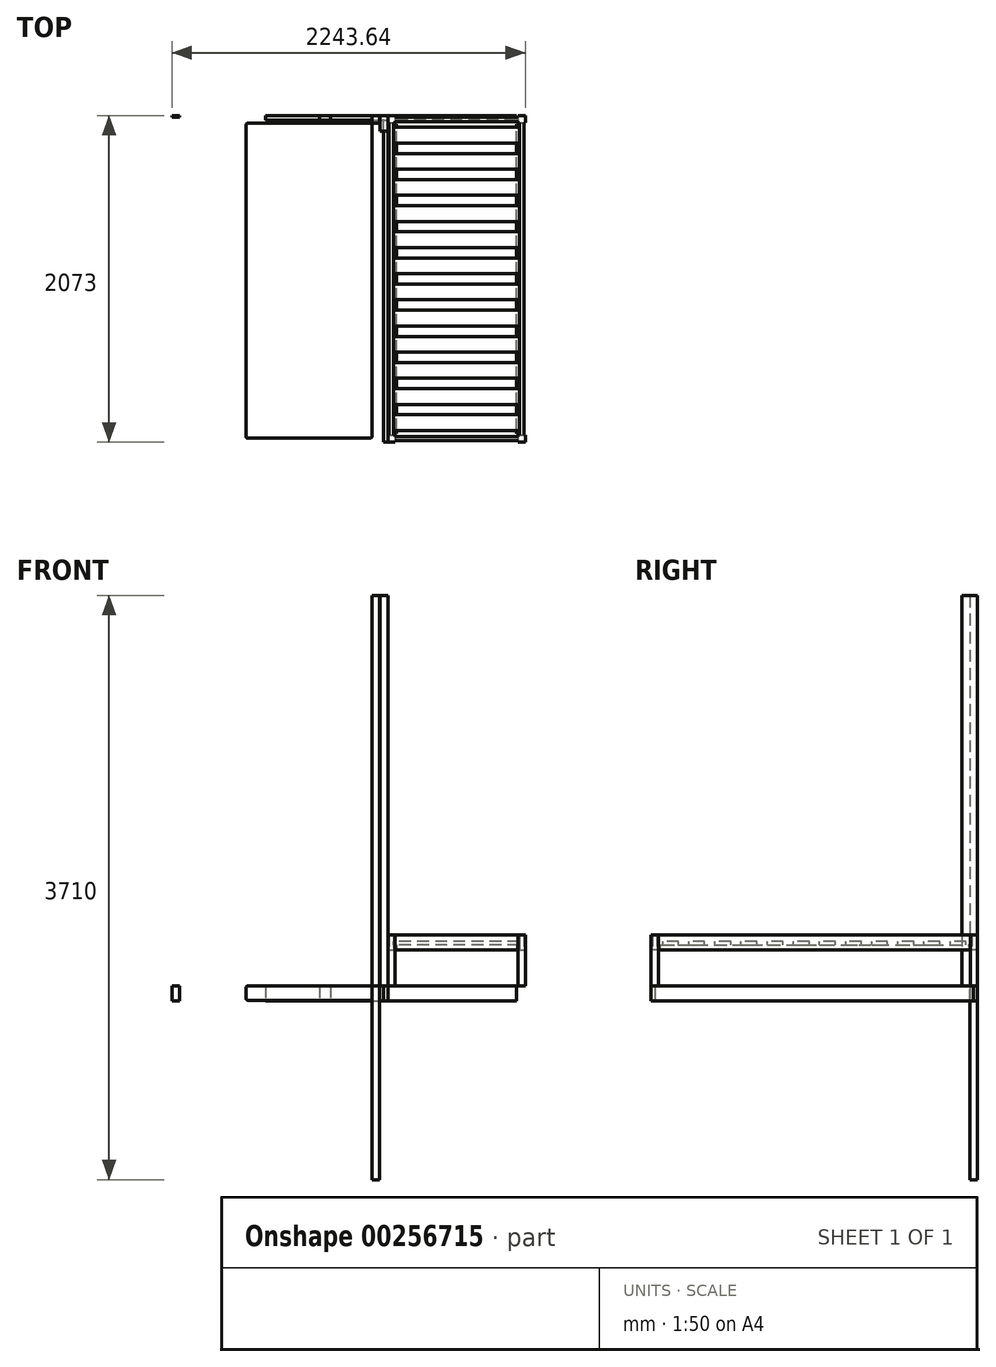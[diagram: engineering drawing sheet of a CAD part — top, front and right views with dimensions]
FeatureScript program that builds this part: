
annotation { "Feature Type Name" : "Feature", "Feature Type Description" : "" }
export const myFeature = defineFeature(function(context is Context, id is Id, definition is map)
    precondition{}
    {
        {
            var Q0;
            Q0=qCreatedBy(makeId("Top.planeOp"),FACE);
            var sketch = newSketch(context, id + "F0", { "sketchPlane" : qUnion([Q0])});
            skLineSegment(sketch, "E0.bottom", {"start": v(0, 0) * mm, "end": v(45, 0) * mm});
            skLineSegment(sketch, "E0.top", {"start": v(0, -45) * mm, "end": v(45, -45) * mm});
            skLineSegment(sketch, "E0.left", {"start": v(0, 0) * mm, "end": v(0, -45) * mm});
            skLineSegment(sketch, "E0.right", {"start": v(45, 0) * mm, "end": v(45, -45) * mm});
            skSolve(sketch);
        }
        {
            var Q0;
            Q0=makeQuery(id+"F0.imprint","IMPRINT",FACE,{"disambiguationData":[TD([[makeQuery(id+"F0.imprint","IMPRINT",EDGE,{"derivedFrom":sQuery(id+"F0.wireOp",EDGE,"E0.bottom")}),-1.0]])]});
            extrude(context, id + "F1", {"entities" : qUnion([Q0]), "depth" : 320 * mm});
        }
        {
            var Q0;
            Q0=makeQuery(id+"F1.opExtrude","SWEPT_BODY",BODY,{"disambiguationData":[OSD([sQuery(id+"F0.wireOp",EDGE,"E0.bottom"),sQuery(id+"F0.wireOp",EDGE,"E0.top"),sQuery(id+"F0.wireOp",EDGE,"E0.left"),sQuery(id+"F0.wireOp",EDGE,"E0.right")])]});
            transform(context, id + "F2", {"entities" : qUnion([Q0]), "transformType" : TransformType.TRANSLATION_3D, "dx" : 845 * mm, "dy" : 0 * mm, "dz" : 0 * mm, "makeCopy" : true});
        }
        {
            var Q0;
            Q0=makeQuery(id+"F1.opExtrude","SWEPT_BODY",BODY,{"disambiguationData":[OSD([sQuery(id+"F0.wireOp",EDGE,"E0.bottom"),sQuery(id+"F0.wireOp",EDGE,"E0.top"),sQuery(id+"F0.wireOp",EDGE,"E0.left"),sQuery(id+"F0.wireOp",EDGE,"E0.right")])]});
            transform(context, id + "F3", {"entities" : qUnion([Q0]), "transformType" : TransformType.TRANSLATION_3D, "dx" : 0 * mm, "dy" : -2045 * mm, "dz" : 0 * mm, "makeCopy" : true});
        }
        {
            var Q0;
            Q0=makeQuery(id+"F2.opPattern","COPY",BODY,{"derivedFrom":makeQuery(id+"F1.opExtrude","SWEPT_BODY",BODY,{"disambiguationData":[OSD([sQuery(id+"F0.wireOp",EDGE,"E0.bottom"),sQuery(id+"F0.wireOp",EDGE,"E0.top"),sQuery(id+"F0.wireOp",EDGE,"E0.left"),sQuery(id+"F0.wireOp",EDGE,"E0.right")])]}),"instanceName":"1"});
            transform(context, id + "F4", {"entities" : qUnion([Q0]), "transformType" : TransformType.TRANSLATION_3D, "dx" : 0 * mm, "dy" : -2045 * mm, "dz" : 0 * mm, "makeCopy" : true});
        }
        {
            var Q0;
            Q0=makeQuery(id+"F1.opExtrude","SWEPT_FACE",FACE,{"disambiguationData":[OSD([sQuery(id+"F0.wireOp",EDGE,"E0.top")])]});
            var sketch = newSketch(context, id + "F5", { "sketchPlane" : qUnion([Q0])});
            skLineSegment(sketch, "E1.bottom", {"start": v(0, 320) * mm, "end": v(28, 320) * mm});
            skLineSegment(sketch, "E1.top", {"start": v(0, 225) * mm, "end": v(28, 225) * mm});
            skLineSegment(sketch, "E1.left", {"start": v(0, 320) * mm, "end": v(0, 225) * mm});
            skLineSegment(sketch, "E1.right", {"start": v(28, 320) * mm, "end": v(28, 225) * mm});
            skSolve(sketch);
        }
        {
            var Q0;
            Q0=makeQuery(id+"F5.imprint","IMPRINT",FACE,{"disambiguationData":[TD([[makeQuery(id+"F5.imprint","IMPRINT",EDGE,{"derivedFrom":sQuery(id+"F5.wireOp",EDGE,"E1.bottom")}),-1.0]])]});
            extrude(context, id + "F6", {"entities" : qUnion([Q0]), "depth" : 2000 * mm});
        }
        {
            var Q0;
            Q0=makeQuery(id+"F6.opExtrude","SWEPT_BODY",BODY,{"disambiguationData":[OSD([sQuery(id+"F5.wireOp",EDGE,"E1.bottom"),sQuery(id+"F5.wireOp",EDGE,"E1.top"),sQuery(id+"F5.wireOp",EDGE,"E1.left"),sQuery(id+"F5.wireOp",EDGE,"E1.right")])]});
            transform(context, id + "F7", {"entities" : qUnion([Q0]), "transformType" : TransformType.TRANSLATION_3D, "dx" : 8.5 * mm, "dy" : 0 * mm, "dz" : 0 * mm, "makeCopy" : false});
        }
        {
            var Q0;
            Q0=makeQuery(id+"F6.opExtrude","SWEPT_BODY",BODY,{"disambiguationData":[OSD([sQuery(id+"F5.wireOp",EDGE,"E1.bottom"),sQuery(id+"F5.wireOp",EDGE,"E1.top"),sQuery(id+"F5.wireOp",EDGE,"E1.left"),sQuery(id+"F5.wireOp",EDGE,"E1.right")])]});
            transform(context, id + "F8", {"entities" : qUnion([Q0]), "transformType" : TransformType.TRANSLATION_3D, "dx" : 828 * mm, "dy" : 0 * mm, "dz" : 0 * mm, "makeCopy" : true});
        }
        {
            var Q0;
            Q0=makeQuery(id+"F2.opPattern","COPY",BODY,{"derivedFrom":makeQuery(id+"F1.opExtrude","SWEPT_BODY",BODY,{"disambiguationData":[OSD([sQuery(id+"F0.wireOp",EDGE,"E0.bottom"),sQuery(id+"F0.wireOp",EDGE,"E0.top"),sQuery(id+"F0.wireOp",EDGE,"E0.left"),sQuery(id+"F0.wireOp",EDGE,"E0.right")])]}),"instanceName":"1"});
            transform(context, id + "F9", {"entities" : qUnion([Q0]), "transformType" : TransformType.TRANSLATION_3D, "dx" : -17 * mm, "dy" : 0 * mm, "dz" : 0 * mm, "makeCopy" : false});
        }
        {
            var Q0;
            Q0=makeQuery(id+"F4.opPattern","COPY",BODY,{"derivedFrom":makeQuery(id+"F2.opPattern","COPY",BODY,{"derivedFrom":makeQuery(id+"F1.opExtrude","SWEPT_BODY",BODY,{"disambiguationData":[OSD([sQuery(id+"F0.wireOp",EDGE,"E0.bottom"),sQuery(id+"F0.wireOp",EDGE,"E0.top"),sQuery(id+"F0.wireOp",EDGE,"E0.left"),sQuery(id+"F0.wireOp",EDGE,"E0.right")])]}),"instanceName":"1"}),"instanceName":"1"});
            transform(context, id + "F10", {"entities" : qUnion([Q0]), "transformType" : TransformType.TRANSLATION_3D, "dx" : -17 * mm, "dy" : 0 * mm, "dz" : 0 * mm, "makeCopy" : false});
        }
        {
            var Q0;
            Q0=makeQuery(id+"F6.opExtrude","SWEPT_BODY",BODY,{"disambiguationData":[OSD([sQuery(id+"F5.wireOp",EDGE,"E1.bottom"),sQuery(id+"F5.wireOp",EDGE,"E1.top"),sQuery(id+"F5.wireOp",EDGE,"E1.left"),sQuery(id+"F5.wireOp",EDGE,"E1.right")])]});
            var Q1;
            Q1=makeQuery(id+"F8.opPattern","COPY",BODY,{"derivedFrom":makeQuery(id+"F6.opExtrude","SWEPT_BODY",BODY,{"disambiguationData":[OSD([sQuery(id+"F5.wireOp",EDGE,"E1.bottom"),sQuery(id+"F5.wireOp",EDGE,"E1.top"),sQuery(id+"F5.wireOp",EDGE,"E1.left"),sQuery(id+"F5.wireOp",EDGE,"E1.right")])]}),"instanceName":"1"});
            deleteBodies(context, id + "F11", {"entities" : qUnion([Q0, Q1])});
        }
        {
            var Q0;
            Q0=makeQuery(id+"F3.opPattern","COPY",BODY,{"derivedFrom":makeQuery(id+"F1.opExtrude","SWEPT_BODY",BODY,{"disambiguationData":[OSD([sQuery(id+"F0.wireOp",EDGE,"E0.bottom"),sQuery(id+"F0.wireOp",EDGE,"E0.top"),sQuery(id+"F0.wireOp",EDGE,"E0.left"),sQuery(id+"F0.wireOp",EDGE,"E0.right")])]}),"instanceName":"1"});
            transform(context, id + "F12", {"entities" : qUnion([Q0]), "transformType" : TransformType.TRANSLATION_3D, "dx" : 0 * mm, "dy" : 17 * mm, "dz" : 0 * mm, "makeCopy" : false});
        }
        {
            var Q0;
            Q0=makeQuery(id+"F4.opPattern","COPY",BODY,{"derivedFrom":makeQuery(id+"F2.opPattern","COPY",BODY,{"derivedFrom":makeQuery(id+"F1.opExtrude","SWEPT_BODY",BODY,{"disambiguationData":[OSD([sQuery(id+"F0.wireOp",EDGE,"E0.bottom"),sQuery(id+"F0.wireOp",EDGE,"E0.top"),sQuery(id+"F0.wireOp",EDGE,"E0.left"),sQuery(id+"F0.wireOp",EDGE,"E0.right")])]}),"instanceName":"1"}),"instanceName":"1"});
            transform(context, id + "F13", {"entities" : qUnion([Q0]), "transformType" : TransformType.TRANSLATION_3D, "dx" : 0 * mm, "dy" : 17 * mm, "dz" : 0 * mm, "makeCopy" : false});
        }
        {
            var Q0;
            Q0=makeQuery(id+"F1.opExtrude","SWEPT_FACE",FACE,{"disambiguationData":[OSD([sQuery(id+"F0.wireOp",EDGE,"E0.top")])]});
            var sketch = newSketch(context, id + "F14", { "sketchPlane" : qUnion([Q0])});
            skLineSegment(sketch, "E2.bottom", {"start": v(0, 320) * mm, "end": v(28, 320) * mm});
            skLineSegment(sketch, "E2.top", {"start": v(0, 230) * mm, "end": v(28, 230) * mm});
            skLineSegment(sketch, "E2.left", {"start": v(0, 320) * mm, "end": v(0, 230) * mm});
            skLineSegment(sketch, "E2.right", {"start": v(28, 320) * mm, "end": v(28, 230) * mm});
            skSolve(sketch);
        }
        {
            var Q0;
            Q0=makeQuery(id+"F14.imprint","IMPRINT",FACE,{"disambiguationData":[TD([[makeQuery(id+"F14.imprint","IMPRINT",EDGE,{"derivedFrom":sQuery(id+"F14.wireOp",EDGE,"E2.bottom")}),-1.0]])]});
            extrude(context, id + "F15", {"entities" : qUnion([Q0]), "depth" : 1983 * mm});
        }
        {
            var Q0;
            Q0=makeQuery(id+"F15.opExtrude","SWEPT_BODY",BODY,{"disambiguationData":[OSD([sQuery(id+"F14.wireOp",EDGE,"E2.bottom"),sQuery(id+"F14.wireOp",EDGE,"E2.top"),sQuery(id+"F14.wireOp",EDGE,"E2.left"),sQuery(id+"F14.wireOp",EDGE,"E2.right")])]});
            transform(context, id + "F16", {"entities" : qUnion([Q0]), "transformType" : TransformType.TRANSLATION_3D, "dx" : 8.5 * mm, "dy" : 0 * mm, "dz" : 0 * mm, "makeCopy" : false});
        }
        {
            var Q0;
            Q0=makeQuery(id+"F15.opExtrude","SWEPT_BODY",BODY,{"disambiguationData":[OSD([sQuery(id+"F14.wireOp",EDGE,"E2.bottom"),sQuery(id+"F14.wireOp",EDGE,"E2.top"),sQuery(id+"F14.wireOp",EDGE,"E2.left"),sQuery(id+"F14.wireOp",EDGE,"E2.right")])]});
            transform(context, id + "F17", {"entities" : qUnion([Q0]), "transformType" : TransformType.TRANSLATION_3D, "dx" : 828 * mm, "dy" : 0 * mm, "dz" : 0 * mm, "makeCopy" : true});
        }
        {
            var Q0;
            Q0=makeQuery(id+"F1.opExtrude","SWEPT_FACE",FACE,{"disambiguationData":[OSD([sQuery(id+"F0.wireOp",EDGE,"E0.right")])]});
            var sketch = newSketch(context, id + "F18", { "sketchPlane" : qUnion([Q0])});
            skLineSegment(sketch, "E3.bottom", {"start": v(0, 320) * mm, "end": v(-28, 320) * mm});
            skLineSegment(sketch, "E3.top", {"start": v(0, 230) * mm, "end": v(-28, 230) * mm});
            skLineSegment(sketch, "E3.left", {"start": v(0, 320) * mm, "end": v(0, 230) * mm});
            skLineSegment(sketch, "E3.right", {"start": v(-28, 320) * mm, "end": v(-28, 230) * mm});
            skSolve(sketch);
        }
        {
            var Q0;
            Q0=makeQuery(id+"F18.imprint","IMPRINT",FACE,{"disambiguationData":[TD([[makeQuery(id+"F18.imprint","IMPRINT",EDGE,{"derivedFrom":sQuery(id+"F18.wireOp",EDGE,"E3.bottom")}),1.0]])]});
            extrude(context, id + "F19", {"entities" : qUnion([Q0]), "depth" : 783 * mm});
        }
        {
            var Q0;
            Q0=makeQuery(id+"F19.opExtrude","SWEPT_BODY",BODY,{"disambiguationData":[OSD([sQuery(id+"F18.wireOp",EDGE,"E3.bottom"),sQuery(id+"F18.wireOp",EDGE,"E3.top"),sQuery(id+"F18.wireOp",EDGE,"E3.left"),sQuery(id+"F18.wireOp",EDGE,"E3.right")])]});
            transform(context, id + "F20", {"entities" : qUnion([Q0]), "transformType" : TransformType.TRANSLATION_3D, "dx" : 0 * mm, "dy" : -8.5 * mm, "dz" : 0 * mm, "makeCopy" : false});
        }
        {
            var Q0;
            Q0=makeQuery(id+"F19.opExtrude","SWEPT_BODY",BODY,{"disambiguationData":[OSD([sQuery(id+"F18.wireOp",EDGE,"E3.bottom"),sQuery(id+"F18.wireOp",EDGE,"E3.top"),sQuery(id+"F18.wireOp",EDGE,"E3.left"),sQuery(id+"F18.wireOp",EDGE,"E3.right")])]});
            transform(context, id + "F21", {"entities" : qUnion([Q0]), "transformType" : TransformType.TRANSLATION_3D, "dx" : 0 * mm, "dy" : -2028 * mm, "dz" : 0 * mm, "makeCopy" : true});
        }
        {
            var Q0;
            Q0=makeQuery(id+"F1.opExtrude","SWEPT_FACE",FACE,{"disambiguationData":[OSD([sQuery(id+"F0.wireOp",EDGE,"E0.top")])]});
            var sketch = newSketch(context, id + "F22", { "sketchPlane" : qUnion([Q0])});
            skLineSegment(sketch, "E4.bottom", {"start": v(45, 320) * mm, "end": v(27, 320) * mm});
            skLineSegment(sketch, "E4.top", {"start": v(45, 288) * mm, "end": v(27, 288) * mm});
            skLineSegment(sketch, "E4.left", {"start": v(45, 320) * mm, "end": v(45, 288) * mm});
            skLineSegment(sketch, "E4.right", {"start": v(27, 320) * mm, "end": v(27, 288) * mm});
            skSolve(sketch);
        }
        {
            var Q0;
            Q0=makeQuery(id+"F22.imprint","IMPRINT",FACE,{"disambiguationData":[TD([[makeQuery(id+"F22.imprint","IMPRINT",EDGE,{"derivedFrom":sQuery(id+"F22.wireOp",EDGE,"E4.bottom")}),-1.0]])]});
            extrude(context, id + "F23", {"entities" : qUnion([Q0]), "depth" : 1963 * mm});
        }
        {
            var Q0;
            Q0=makeQuery(id+"F23.opExtrude","SWEPT_BODY",BODY,{"disambiguationData":[OSD([sQuery(id+"F22.wireOp",EDGE,"E4.bottom"),sQuery(id+"F22.wireOp",EDGE,"E4.top"),sQuery(id+"F22.wireOp",EDGE,"E4.left"),sQuery(id+"F22.wireOp",EDGE,"E4.right")])]});
            transform(context, id + "F24", {"entities" : qUnion([Q0]), "transformType" : TransformType.TRANSLATION_3D, "dx" : 9.5 * mm, "dy" : -10 * mm, "dz" : -58 * mm, "makeCopy" : false});
        }
        {
            var Q0;
            Q0=makeQuery(id+"F23.opExtrude","SWEPT_BODY",BODY,{"disambiguationData":[OSD([sQuery(id+"F22.wireOp",EDGE,"E4.bottom"),sQuery(id+"F22.wireOp",EDGE,"E4.top"),sQuery(id+"F22.wireOp",EDGE,"E4.left"),sQuery(id+"F22.wireOp",EDGE,"E4.right")])]});
            transform(context, id + "F25", {"entities" : qUnion([Q0]), "transformType" : TransformType.TRANSLATION_3D, "dx" : 782 * mm, "dy" : 0 * mm, "dz" : 0 * mm, "makeCopy" : true});
        }
        {
            var Q0;
            Q0=makeQuery(id+"F23.opExtrude","SWEPT_FACE",FACE,{"disambiguationData":[OSD([sQuery(id+"F22.wireOp",EDGE,"E4.left")])]});
            var sketch = newSketch(context, id + "F26", { "sketchPlane" : qUnion([Q0])});
            skLineSegment(sketch, "E5.bottom", {"start": v(-55, 262) * mm, "end": v(-155, 262) * mm});
            skLineSegment(sketch, "E5.top", {"start": v(-55, 284) * mm, "end": v(-155, 284) * mm});
            skLineSegment(sketch, "E5.left", {"start": v(-55, 262) * mm, "end": v(-55, 284) * mm});
            skLineSegment(sketch, "E5.right", {"start": v(-155, 262) * mm, "end": v(-155, 284) * mm});
            skSolve(sketch);
        }
        {
            var Q0;
            Q0=makeQuery(id+"F26.imprint","IMPRINT",FACE,{"disambiguationData":[TD([[makeQuery(id+"F26.imprint","IMPRINT",EDGE,{"derivedFrom":sQuery(id+"F26.wireOp",EDGE,"E5.bottom")}),1.0]])]});
            extrude(context, id + "F27", {"entities" : qUnion([Q0]), "depth" : 800 * mm});
        }
        {
            var Q0;
            Q0=makeQuery(id+"F27.opExtrude","SWEPT_BODY",BODY,{"disambiguationData":[OSD([sQuery(id+"F26.wireOp",EDGE,"E5.bottom"),sQuery(id+"F26.wireOp",EDGE,"E5.top"),sQuery(id+"F26.wireOp",EDGE,"E5.left"),sQuery(id+"F26.wireOp",EDGE,"E5.right")])]});
            transform(context, id + "F28", {"entities" : qUnion([Q0]), "transformType" : TransformType.TRANSLATION_3D, "dx" : -18 * mm, "dy" : 0 * mm, "dz" : 0 * mm, "makeCopy" : false});
        }
        {
            var Q0;
            Q0=makeQuery(id+"F27.opExtrude","SWEPT_BODY",BODY,{"disambiguationData":[OSD([sQuery(id+"F26.wireOp",EDGE,"E5.bottom"),sQuery(id+"F26.wireOp",EDGE,"E5.top"),sQuery(id+"F26.wireOp",EDGE,"E5.left"),sQuery(id+"F26.wireOp",EDGE,"E5.right")])]});
            transform(context, id + "F29", {"entities" : qUnion([Q0]), "transformType" : TransformType.TRANSLATION_3D, "dx" : 0 * mm, "dy" : -21.5 * mm, "dz" : 0 * mm, "makeCopy" : false});
        }
        {
            var Q0;
            Q0=makeQuery(id+"F27.opExtrude","SWEPT_BODY",BODY,{"disambiguationData":[OSD([sQuery(id+"F26.wireOp",EDGE,"E5.bottom"),sQuery(id+"F26.wireOp",EDGE,"E5.top"),sQuery(id+"F26.wireOp",EDGE,"E5.left"),sQuery(id+"F26.wireOp",EDGE,"E5.right")])]});
            transform(context, id + "F30", {"entities" : qUnion([Q0]), "transformType" : TransformType.TRANSLATION_3D, "dx" : 0 * mm, "dy" : -160 * mm, "dz" : 0 * mm, "makeCopy" : true});
        }
        {
            var Q0;
            Q0=makeQuery(id+"F30.opPattern","COPY",BODY,{"derivedFrom":makeQuery(id+"F27.opExtrude","SWEPT_BODY",BODY,{"disambiguationData":[OSD([sQuery(id+"F26.wireOp",EDGE,"E5.bottom"),sQuery(id+"F26.wireOp",EDGE,"E5.top"),sQuery(id+"F26.wireOp",EDGE,"E5.left"),sQuery(id+"F26.wireOp",EDGE,"E5.right")])]}),"instanceName":"1"});
            transform(context, id + "F31", {"entities" : qUnion([Q0]), "transformType" : TransformType.TRANSLATION_3D, "dx" : 0 * mm, "dy" : -160 * mm, "dz" : 0 * mm, "makeCopy" : false});
        }
        {
            var Q0;
            Q0=makeQuery(id+"F27.opExtrude","SWEPT_BODY",BODY,{"disambiguationData":[OSD([sQuery(id+"F26.wireOp",EDGE,"E5.bottom"),sQuery(id+"F26.wireOp",EDGE,"E5.top"),sQuery(id+"F26.wireOp",EDGE,"E5.left"),sQuery(id+"F26.wireOp",EDGE,"E5.right")])]});
            transform(context, id + "F32", {"entities" : qUnion([Q0]), "transformType" : TransformType.TRANSLATION_3D, "dx" : 0 * mm, "dy" : -160 * mm, "dz" : 0 * mm, "makeCopy" : true});
        }
        {
            var Q0;
            Q0=makeQuery(id+"F30.opPattern","COPY",BODY,{"derivedFrom":makeQuery(id+"F27.opExtrude","SWEPT_BODY",BODY,{"disambiguationData":[OSD([sQuery(id+"F26.wireOp",EDGE,"E5.bottom"),sQuery(id+"F26.wireOp",EDGE,"E5.top"),sQuery(id+"F26.wireOp",EDGE,"E5.left"),sQuery(id+"F26.wireOp",EDGE,"E5.right")])]}),"instanceName":"1"});
            transform(context, id + "F33", {"entities" : qUnion([Q0]), "transformType" : TransformType.TRANSLATION_3D, "dx" : 0 * mm, "dy" : -160 * mm, "dz" : 0 * mm, "makeCopy" : true});
        }
        {
            var Q0;
            Q0=makeQuery(id+"F33.opPattern","COPY",BODY,{"derivedFrom":makeQuery(id+"F30.opPattern","COPY",BODY,{"derivedFrom":makeQuery(id+"F27.opExtrude","SWEPT_BODY",BODY,{"disambiguationData":[OSD([sQuery(id+"F26.wireOp",EDGE,"E5.bottom"),sQuery(id+"F26.wireOp",EDGE,"E5.top"),sQuery(id+"F26.wireOp",EDGE,"E5.left"),sQuery(id+"F26.wireOp",EDGE,"E5.right")])]}),"instanceName":"1"}),"instanceName":"1"});
            transform(context, id + "F34", {"entities" : qUnion([Q0]), "transformType" : TransformType.TRANSLATION_3D, "dx" : 0 * mm, "dy" : -160 * mm, "dz" : 0 * mm, "makeCopy" : true});
        }
        {
            var Q0;
            Q0=makeQuery(id+"F34.opPattern","COPY",BODY,{"derivedFrom":makeQuery(id+"F33.opPattern","COPY",BODY,{"derivedFrom":makeQuery(id+"F30.opPattern","COPY",BODY,{"derivedFrom":makeQuery(id+"F27.opExtrude","SWEPT_BODY",BODY,{"disambiguationData":[OSD([sQuery(id+"F26.wireOp",EDGE,"E5.bottom"),sQuery(id+"F26.wireOp",EDGE,"E5.top"),sQuery(id+"F26.wireOp",EDGE,"E5.left"),sQuery(id+"F26.wireOp",EDGE,"E5.right")])]}),"instanceName":"1"}),"instanceName":"1"}),"instanceName":"1"});
            transform(context, id + "F35", {"entities" : qUnion([Q0]), "transformType" : TransformType.TRANSLATION_3D, "dx" : 0 * mm, "dy" : -160 * mm, "dz" : 0 * mm, "makeCopy" : true});
        }
        {
            var Q0;
            Q0=makeQuery(id+"F35.opPattern","COPY",BODY,{"derivedFrom":makeQuery(id+"F34.opPattern","COPY",BODY,{"derivedFrom":makeQuery(id+"F33.opPattern","COPY",BODY,{"derivedFrom":makeQuery(id+"F30.opPattern","COPY",BODY,{"derivedFrom":makeQuery(id+"F27.opExtrude","SWEPT_BODY",BODY,{"disambiguationData":[OSD([sQuery(id+"F26.wireOp",EDGE,"E5.bottom"),sQuery(id+"F26.wireOp",EDGE,"E5.top"),sQuery(id+"F26.wireOp",EDGE,"E5.left"),sQuery(id+"F26.wireOp",EDGE,"E5.right")])]}),"instanceName":"1"}),"instanceName":"1"}),"instanceName":"1"}),"instanceName":"1"});
            transform(context, id + "F36", {"entities" : qUnion([Q0]), "transformType" : TransformType.TRANSLATION_3D, "dx" : 0 * mm, "dy" : -160 * mm, "dz" : 0 * mm, "makeCopy" : true});
        }
        {
            var Q0;
            Q0=makeQuery(id+"F36.opPattern","COPY",BODY,{"derivedFrom":makeQuery(id+"F35.opPattern","COPY",BODY,{"derivedFrom":makeQuery(id+"F34.opPattern","COPY",BODY,{"derivedFrom":makeQuery(id+"F33.opPattern","COPY",BODY,{"derivedFrom":makeQuery(id+"F30.opPattern","COPY",BODY,{"derivedFrom":makeQuery(id+"F27.opExtrude","SWEPT_BODY",BODY,{"disambiguationData":[OSD([sQuery(id+"F26.wireOp",EDGE,"E5.bottom"),sQuery(id+"F26.wireOp",EDGE,"E5.top"),sQuery(id+"F26.wireOp",EDGE,"E5.left"),sQuery(id+"F26.wireOp",EDGE,"E5.right")])]}),"instanceName":"1"}),"instanceName":"1"}),"instanceName":"1"}),"instanceName":"1"}),"instanceName":"1"});
            transform(context, id + "F37", {"entities" : qUnion([Q0]), "transformType" : TransformType.TRANSLATION_3D, "dx" : 0 * mm, "dy" : -160 * mm, "dz" : 0 * mm, "makeCopy" : true});
        }
        {
            var Q0;
            Q0=makeQuery(id+"F37.opPattern","COPY",BODY,{"derivedFrom":makeQuery(id+"F36.opPattern","COPY",BODY,{"derivedFrom":makeQuery(id+"F35.opPattern","COPY",BODY,{"derivedFrom":makeQuery(id+"F34.opPattern","COPY",BODY,{"derivedFrom":makeQuery(id+"F33.opPattern","COPY",BODY,{"derivedFrom":makeQuery(id+"F30.opPattern","COPY",BODY,{"derivedFrom":makeQuery(id+"F27.opExtrude","SWEPT_BODY",BODY,{"disambiguationData":[OSD([sQuery(id+"F26.wireOp",EDGE,"E5.bottom"),sQuery(id+"F26.wireOp",EDGE,"E5.top"),sQuery(id+"F26.wireOp",EDGE,"E5.left"),sQuery(id+"F26.wireOp",EDGE,"E5.right")])]}),"instanceName":"1"}),"instanceName":"1"}),"instanceName":"1"}),"instanceName":"1"}),"instanceName":"1"}),"instanceName":"1"});
            transform(context, id + "F38", {"entities" : qUnion([Q0]), "transformType" : TransformType.TRANSLATION_3D, "dx" : 0 * mm, "dy" : -160 * mm, "dz" : 0 * mm, "makeCopy" : true});
        }
        {
            var Q0;
            Q0=makeQuery(id+"F38.opPattern","COPY",BODY,{"derivedFrom":makeQuery(id+"F37.opPattern","COPY",BODY,{"derivedFrom":makeQuery(id+"F36.opPattern","COPY",BODY,{"derivedFrom":makeQuery(id+"F35.opPattern","COPY",BODY,{"derivedFrom":makeQuery(id+"F34.opPattern","COPY",BODY,{"derivedFrom":makeQuery(id+"F33.opPattern","COPY",BODY,{"derivedFrom":makeQuery(id+"F30.opPattern","COPY",BODY,{"derivedFrom":makeQuery(id+"F27.opExtrude","SWEPT_BODY",BODY,{"disambiguationData":[OSD([sQuery(id+"F26.wireOp",EDGE,"E5.bottom"),sQuery(id+"F26.wireOp",EDGE,"E5.top"),sQuery(id+"F26.wireOp",EDGE,"E5.left"),sQuery(id+"F26.wireOp",EDGE,"E5.right")])]}),"instanceName":"1"}),"instanceName":"1"}),"instanceName":"1"}),"instanceName":"1"}),"instanceName":"1"}),"instanceName":"1"}),"instanceName":"1"});
            transform(context, id + "F39", {"entities" : qUnion([Q0]), "transformType" : TransformType.TRANSLATION_3D, "dx" : 0 * mm, "dy" : -160 * mm, "dz" : 0 * mm, "makeCopy" : true});
        }
        {
            var Q0;
            Q0=makeQuery(id+"F39.opPattern","COPY",BODY,{"derivedFrom":makeQuery(id+"F38.opPattern","COPY",BODY,{"derivedFrom":makeQuery(id+"F37.opPattern","COPY",BODY,{"derivedFrom":makeQuery(id+"F36.opPattern","COPY",BODY,{"derivedFrom":makeQuery(id+"F35.opPattern","COPY",BODY,{"derivedFrom":makeQuery(id+"F34.opPattern","COPY",BODY,{"derivedFrom":makeQuery(id+"F33.opPattern","COPY",BODY,{"derivedFrom":makeQuery(id+"F30.opPattern","COPY",BODY,{"derivedFrom":makeQuery(id+"F27.opExtrude","SWEPT_BODY",BODY,{"disambiguationData":[OSD([sQuery(id+"F26.wireOp",EDGE,"E5.bottom"),sQuery(id+"F26.wireOp",EDGE,"E5.top"),sQuery(id+"F26.wireOp",EDGE,"E5.left"),sQuery(id+"F26.wireOp",EDGE,"E5.right")])]}),"instanceName":"1"}),"instanceName":"1"}),"instanceName":"1"}),"instanceName":"1"}),"instanceName":"1"}),"instanceName":"1"}),"instanceName":"1"}),"instanceName":"1"});
            transform(context, id + "F40", {"entities" : qUnion([Q0]), "transformType" : TransformType.TRANSLATION_3D, "dx" : 0 * mm, "dy" : -160 * mm, "dz" : 0 * mm, "makeCopy" : true});
        }
        {
            var Q0;
            Q0=makeQuery(id+"F40.opPattern","COPY",BODY,{"derivedFrom":makeQuery(id+"F39.opPattern","COPY",BODY,{"derivedFrom":makeQuery(id+"F38.opPattern","COPY",BODY,{"derivedFrom":makeQuery(id+"F37.opPattern","COPY",BODY,{"derivedFrom":makeQuery(id+"F36.opPattern","COPY",BODY,{"derivedFrom":makeQuery(id+"F35.opPattern","COPY",BODY,{"derivedFrom":makeQuery(id+"F34.opPattern","COPY",BODY,{"derivedFrom":makeQuery(id+"F33.opPattern","COPY",BODY,{"derivedFrom":makeQuery(id+"F30.opPattern","COPY",BODY,{"derivedFrom":makeQuery(id+"F27.opExtrude","SWEPT_BODY",BODY,{"disambiguationData":[OSD([sQuery(id+"F26.wireOp",EDGE,"E5.bottom"),sQuery(id+"F26.wireOp",EDGE,"E5.top"),sQuery(id+"F26.wireOp",EDGE,"E5.left"),sQuery(id+"F26.wireOp",EDGE,"E5.right")])]}),"instanceName":"1"}),"instanceName":"1"}),"instanceName":"1"}),"instanceName":"1"}),"instanceName":"1"}),"instanceName":"1"}),"instanceName":"1"}),"instanceName":"1"}),"instanceName":"1"});
            transform(context, id + "F41", {"entities" : qUnion([Q0]), "transformType" : TransformType.TRANSLATION_3D, "dx" : 0 * mm, "dy" : -160 * mm, "dz" : 0 * mm, "makeCopy" : true});
        }
        {
            var Q0;
            Q0=makeQuery(id+"F41.opPattern","COPY",BODY,{"derivedFrom":makeQuery(id+"F40.opPattern","COPY",BODY,{"derivedFrom":makeQuery(id+"F39.opPattern","COPY",BODY,{"derivedFrom":makeQuery(id+"F38.opPattern","COPY",BODY,{"derivedFrom":makeQuery(id+"F37.opPattern","COPY",BODY,{"derivedFrom":makeQuery(id+"F36.opPattern","COPY",BODY,{"derivedFrom":makeQuery(id+"F35.opPattern","COPY",BODY,{"derivedFrom":makeQuery(id+"F34.opPattern","COPY",BODY,{"derivedFrom":makeQuery(id+"F33.opPattern","COPY",BODY,{"derivedFrom":makeQuery(id+"F30.opPattern","COPY",BODY,{"derivedFrom":makeQuery(id+"F27.opExtrude","SWEPT_BODY",BODY,{"disambiguationData":[OSD([sQuery(id+"F26.wireOp",EDGE,"E5.bottom"),sQuery(id+"F26.wireOp",EDGE,"E5.top"),sQuery(id+"F26.wireOp",EDGE,"E5.left"),sQuery(id+"F26.wireOp",EDGE,"E5.right")])]}),"instanceName":"1"}),"instanceName":"1"}),"instanceName":"1"}),"instanceName":"1"}),"instanceName":"1"}),"instanceName":"1"}),"instanceName":"1"}),"instanceName":"1"}),"instanceName":"1"}),"instanceName":"1"});
            var Q1;
            Q1=makeQuery(id+"F40.opPattern","COPY",BODY,{"derivedFrom":makeQuery(id+"F39.opPattern","COPY",BODY,{"derivedFrom":makeQuery(id+"F38.opPattern","COPY",BODY,{"derivedFrom":makeQuery(id+"F37.opPattern","COPY",BODY,{"derivedFrom":makeQuery(id+"F36.opPattern","COPY",BODY,{"derivedFrom":makeQuery(id+"F35.opPattern","COPY",BODY,{"derivedFrom":makeQuery(id+"F34.opPattern","COPY",BODY,{"derivedFrom":makeQuery(id+"F33.opPattern","COPY",BODY,{"derivedFrom":makeQuery(id+"F30.opPattern","COPY",BODY,{"derivedFrom":makeQuery(id+"F27.opExtrude","SWEPT_BODY",BODY,{"disambiguationData":[OSD([sQuery(id+"F26.wireOp",EDGE,"E5.bottom"),sQuery(id+"F26.wireOp",EDGE,"E5.top"),sQuery(id+"F26.wireOp",EDGE,"E5.left"),sQuery(id+"F26.wireOp",EDGE,"E5.right")])]}),"instanceName":"1"}),"instanceName":"1"}),"instanceName":"1"}),"instanceName":"1"}),"instanceName":"1"}),"instanceName":"1"}),"instanceName":"1"}),"instanceName":"1"}),"instanceName":"1"});
            var Q2;
            Q2=makeQuery(id+"F39.opPattern","COPY",BODY,{"derivedFrom":makeQuery(id+"F38.opPattern","COPY",BODY,{"derivedFrom":makeQuery(id+"F37.opPattern","COPY",BODY,{"derivedFrom":makeQuery(id+"F36.opPattern","COPY",BODY,{"derivedFrom":makeQuery(id+"F35.opPattern","COPY",BODY,{"derivedFrom":makeQuery(id+"F34.opPattern","COPY",BODY,{"derivedFrom":makeQuery(id+"F33.opPattern","COPY",BODY,{"derivedFrom":makeQuery(id+"F30.opPattern","COPY",BODY,{"derivedFrom":makeQuery(id+"F27.opExtrude","SWEPT_BODY",BODY,{"disambiguationData":[OSD([sQuery(id+"F26.wireOp",EDGE,"E5.bottom"),sQuery(id+"F26.wireOp",EDGE,"E5.top"),sQuery(id+"F26.wireOp",EDGE,"E5.left"),sQuery(id+"F26.wireOp",EDGE,"E5.right")])]}),"instanceName":"1"}),"instanceName":"1"}),"instanceName":"1"}),"instanceName":"1"}),"instanceName":"1"}),"instanceName":"1"}),"instanceName":"1"}),"instanceName":"1"});
            var Q3;
            Q3=makeQuery(id+"F38.opPattern","COPY",BODY,{"derivedFrom":makeQuery(id+"F37.opPattern","COPY",BODY,{"derivedFrom":makeQuery(id+"F36.opPattern","COPY",BODY,{"derivedFrom":makeQuery(id+"F35.opPattern","COPY",BODY,{"derivedFrom":makeQuery(id+"F34.opPattern","COPY",BODY,{"derivedFrom":makeQuery(id+"F33.opPattern","COPY",BODY,{"derivedFrom":makeQuery(id+"F30.opPattern","COPY",BODY,{"derivedFrom":makeQuery(id+"F27.opExtrude","SWEPT_BODY",BODY,{"disambiguationData":[OSD([sQuery(id+"F26.wireOp",EDGE,"E5.bottom"),sQuery(id+"F26.wireOp",EDGE,"E5.top"),sQuery(id+"F26.wireOp",EDGE,"E5.left"),sQuery(id+"F26.wireOp",EDGE,"E5.right")])]}),"instanceName":"1"}),"instanceName":"1"}),"instanceName":"1"}),"instanceName":"1"}),"instanceName":"1"}),"instanceName":"1"}),"instanceName":"1"});
            var Q4;
            Q4=makeQuery(id+"F37.opPattern","COPY",BODY,{"derivedFrom":makeQuery(id+"F36.opPattern","COPY",BODY,{"derivedFrom":makeQuery(id+"F35.opPattern","COPY",BODY,{"derivedFrom":makeQuery(id+"F34.opPattern","COPY",BODY,{"derivedFrom":makeQuery(id+"F33.opPattern","COPY",BODY,{"derivedFrom":makeQuery(id+"F30.opPattern","COPY",BODY,{"derivedFrom":makeQuery(id+"F27.opExtrude","SWEPT_BODY",BODY,{"disambiguationData":[OSD([sQuery(id+"F26.wireOp",EDGE,"E5.bottom"),sQuery(id+"F26.wireOp",EDGE,"E5.top"),sQuery(id+"F26.wireOp",EDGE,"E5.left"),sQuery(id+"F26.wireOp",EDGE,"E5.right")])]}),"instanceName":"1"}),"instanceName":"1"}),"instanceName":"1"}),"instanceName":"1"}),"instanceName":"1"}),"instanceName":"1"});
            var Q5;
            Q5=makeQuery(id+"F36.opPattern","COPY",BODY,{"derivedFrom":makeQuery(id+"F35.opPattern","COPY",BODY,{"derivedFrom":makeQuery(id+"F34.opPattern","COPY",BODY,{"derivedFrom":makeQuery(id+"F33.opPattern","COPY",BODY,{"derivedFrom":makeQuery(id+"F30.opPattern","COPY",BODY,{"derivedFrom":makeQuery(id+"F27.opExtrude","SWEPT_BODY",BODY,{"disambiguationData":[OSD([sQuery(id+"F26.wireOp",EDGE,"E5.bottom"),sQuery(id+"F26.wireOp",EDGE,"E5.top"),sQuery(id+"F26.wireOp",EDGE,"E5.left"),sQuery(id+"F26.wireOp",EDGE,"E5.right")])]}),"instanceName":"1"}),"instanceName":"1"}),"instanceName":"1"}),"instanceName":"1"}),"instanceName":"1"});
            var Q6;
            Q6=makeQuery(id+"F35.opPattern","COPY",BODY,{"derivedFrom":makeQuery(id+"F34.opPattern","COPY",BODY,{"derivedFrom":makeQuery(id+"F33.opPattern","COPY",BODY,{"derivedFrom":makeQuery(id+"F30.opPattern","COPY",BODY,{"derivedFrom":makeQuery(id+"F27.opExtrude","SWEPT_BODY",BODY,{"disambiguationData":[OSD([sQuery(id+"F26.wireOp",EDGE,"E5.bottom"),sQuery(id+"F26.wireOp",EDGE,"E5.top"),sQuery(id+"F26.wireOp",EDGE,"E5.left"),sQuery(id+"F26.wireOp",EDGE,"E5.right")])]}),"instanceName":"1"}),"instanceName":"1"}),"instanceName":"1"}),"instanceName":"1"});
            var Q7;
            Q7=makeQuery(id+"F34.opPattern","COPY",BODY,{"derivedFrom":makeQuery(id+"F33.opPattern","COPY",BODY,{"derivedFrom":makeQuery(id+"F30.opPattern","COPY",BODY,{"derivedFrom":makeQuery(id+"F27.opExtrude","SWEPT_BODY",BODY,{"disambiguationData":[OSD([sQuery(id+"F26.wireOp",EDGE,"E5.bottom"),sQuery(id+"F26.wireOp",EDGE,"E5.top"),sQuery(id+"F26.wireOp",EDGE,"E5.left"),sQuery(id+"F26.wireOp",EDGE,"E5.right")])]}),"instanceName":"1"}),"instanceName":"1"}),"instanceName":"1"});
            var Q8;
            Q8=makeQuery(id+"F33.opPattern","COPY",BODY,{"derivedFrom":makeQuery(id+"F30.opPattern","COPY",BODY,{"derivedFrom":makeQuery(id+"F27.opExtrude","SWEPT_BODY",BODY,{"disambiguationData":[OSD([sQuery(id+"F26.wireOp",EDGE,"E5.bottom"),sQuery(id+"F26.wireOp",EDGE,"E5.top"),sQuery(id+"F26.wireOp",EDGE,"E5.left"),sQuery(id+"F26.wireOp",EDGE,"E5.right")])]}),"instanceName":"1"}),"instanceName":"1"});
            var Q9;
            Q9=makeQuery(id+"F32.opPattern","COPY",BODY,{"derivedFrom":makeQuery(id+"F27.opExtrude","SWEPT_BODY",BODY,{"disambiguationData":[OSD([sQuery(id+"F26.wireOp",EDGE,"E5.bottom"),sQuery(id+"F26.wireOp",EDGE,"E5.top"),sQuery(id+"F26.wireOp",EDGE,"E5.left"),sQuery(id+"F26.wireOp",EDGE,"E5.right")])]}),"instanceName":"1"});
            var Q10;
            Q10=makeQuery(id+"F30.opPattern","COPY",BODY,{"derivedFrom":makeQuery(id+"F27.opExtrude","SWEPT_BODY",BODY,{"disambiguationData":[OSD([sQuery(id+"F26.wireOp",EDGE,"E5.bottom"),sQuery(id+"F26.wireOp",EDGE,"E5.top"),sQuery(id+"F26.wireOp",EDGE,"E5.left"),sQuery(id+"F26.wireOp",EDGE,"E5.right")])]}),"instanceName":"1"});
            deleteBodies(context, id + "F42", {"entities" : qUnion([Q0, Q1, Q2, Q3, Q4, Q5, Q6, Q7, Q8, Q9, Q10])});
        }
        {
            var Q0;
            Q0=makeQuery(id+"F27.opExtrude","SWEPT_BODY",BODY,{"disambiguationData":[OSD([sQuery(id+"F26.wireOp",EDGE,"E5.bottom"),sQuery(id+"F26.wireOp",EDGE,"E5.top"),sQuery(id+"F26.wireOp",EDGE,"E5.left"),sQuery(id+"F26.wireOp",EDGE,"E5.right")])]});
            transform(context, id + "F43", {"entities" : qUnion([Q0]), "transformType" : TransformType.TRANSLATION_3D, "dx" : 0 * mm, "dy" : 3 * mm, "dz" : 0 * mm, "makeCopy" : false});
        }
        {
            var Q0;
            Q0=makeQuery(id+"F27.opExtrude","SWEPT_BODY",BODY,{"disambiguationData":[OSD([sQuery(id+"F26.wireOp",EDGE,"E5.bottom"),sQuery(id+"F26.wireOp",EDGE,"E5.top"),sQuery(id+"F26.wireOp",EDGE,"E5.left"),sQuery(id+"F26.wireOp",EDGE,"E5.right")])]});
            transform(context, id + "F44", {"entities" : qUnion([Q0]), "transformType" : TransformType.TRANSLATION_3D, "dx" : 0 * mm, "dy" : -166 * mm, "dz" : 0 * mm, "makeCopy" : true});
        }
        {
            var Q0;
            Q0=makeQuery(id+"F44.opPattern","COPY",BODY,{"derivedFrom":makeQuery(id+"F27.opExtrude","SWEPT_BODY",BODY,{"disambiguationData":[OSD([sQuery(id+"F26.wireOp",EDGE,"E5.bottom"),sQuery(id+"F26.wireOp",EDGE,"E5.top"),sQuery(id+"F26.wireOp",EDGE,"E5.left"),sQuery(id+"F26.wireOp",EDGE,"E5.right")])]}),"instanceName":"1"});
            transform(context, id + "F45", {"entities" : qUnion([Q0]), "transformType" : TransformType.TRANSLATION_3D, "dx" : 0 * mm, "dy" : -166 * mm, "dz" : 0 * mm, "makeCopy" : true});
        }
        {
            var Q0;
            Q0=makeQuery(id+"F45.opPattern","COPY",BODY,{"derivedFrom":makeQuery(id+"F44.opPattern","COPY",BODY,{"derivedFrom":makeQuery(id+"F27.opExtrude","SWEPT_BODY",BODY,{"disambiguationData":[OSD([sQuery(id+"F26.wireOp",EDGE,"E5.bottom"),sQuery(id+"F26.wireOp",EDGE,"E5.top"),sQuery(id+"F26.wireOp",EDGE,"E5.left"),sQuery(id+"F26.wireOp",EDGE,"E5.right")])]}),"instanceName":"1"}),"instanceName":"1"});
            transform(context, id + "F46", {"entities" : qUnion([Q0]), "transformType" : TransformType.TRANSLATION_3D, "dx" : 0 * mm, "dy" : -166 * mm, "dz" : 0 * mm, "makeCopy" : true});
        }
        {
            var Q0;
            Q0=makeQuery(id+"F46.opPattern","COPY",BODY,{"derivedFrom":makeQuery(id+"F45.opPattern","COPY",BODY,{"derivedFrom":makeQuery(id+"F44.opPattern","COPY",BODY,{"derivedFrom":makeQuery(id+"F27.opExtrude","SWEPT_BODY",BODY,{"disambiguationData":[OSD([sQuery(id+"F26.wireOp",EDGE,"E5.bottom"),sQuery(id+"F26.wireOp",EDGE,"E5.top"),sQuery(id+"F26.wireOp",EDGE,"E5.left"),sQuery(id+"F26.wireOp",EDGE,"E5.right")])]}),"instanceName":"1"}),"instanceName":"1"}),"instanceName":"1"});
            transform(context, id + "F47", {"entities" : qUnion([Q0]), "transformType" : TransformType.TRANSLATION_3D, "dx" : 0 * mm, "dy" : -166 * mm, "dz" : 0 * mm, "makeCopy" : true});
        }
        {
            var Q0;
            Q0=makeQuery(id+"F47.opPattern","COPY",BODY,{"derivedFrom":makeQuery(id+"F46.opPattern","COPY",BODY,{"derivedFrom":makeQuery(id+"F45.opPattern","COPY",BODY,{"derivedFrom":makeQuery(id+"F44.opPattern","COPY",BODY,{"derivedFrom":makeQuery(id+"F27.opExtrude","SWEPT_BODY",BODY,{"disambiguationData":[OSD([sQuery(id+"F26.wireOp",EDGE,"E5.bottom"),sQuery(id+"F26.wireOp",EDGE,"E5.top"),sQuery(id+"F26.wireOp",EDGE,"E5.left"),sQuery(id+"F26.wireOp",EDGE,"E5.right")])]}),"instanceName":"1"}),"instanceName":"1"}),"instanceName":"1"}),"instanceName":"1"});
            transform(context, id + "F48", {"entities" : qUnion([Q0]), "transformType" : TransformType.TRANSLATION_3D, "dx" : 0 * mm, "dy" : -166 * mm, "dz" : 0 * mm, "makeCopy" : true});
        }
        {
            var Q0;
            Q0=makeQuery(id+"F48.opPattern","COPY",BODY,{"derivedFrom":makeQuery(id+"F47.opPattern","COPY",BODY,{"derivedFrom":makeQuery(id+"F46.opPattern","COPY",BODY,{"derivedFrom":makeQuery(id+"F45.opPattern","COPY",BODY,{"derivedFrom":makeQuery(id+"F44.opPattern","COPY",BODY,{"derivedFrom":makeQuery(id+"F27.opExtrude","SWEPT_BODY",BODY,{"disambiguationData":[OSD([sQuery(id+"F26.wireOp",EDGE,"E5.bottom"),sQuery(id+"F26.wireOp",EDGE,"E5.top"),sQuery(id+"F26.wireOp",EDGE,"E5.left"),sQuery(id+"F26.wireOp",EDGE,"E5.right")])]}),"instanceName":"1"}),"instanceName":"1"}),"instanceName":"1"}),"instanceName":"1"}),"instanceName":"1"});
            transform(context, id + "F49", {"entities" : qUnion([Q0]), "transformType" : TransformType.TRANSLATION_3D, "dx" : 0 * mm, "dy" : -166 * mm, "dz" : 0 * mm, "makeCopy" : true});
        }
        {
            var Q0;
            Q0=makeQuery(id+"F49.opPattern","COPY",BODY,{"derivedFrom":makeQuery(id+"F48.opPattern","COPY",BODY,{"derivedFrom":makeQuery(id+"F47.opPattern","COPY",BODY,{"derivedFrom":makeQuery(id+"F46.opPattern","COPY",BODY,{"derivedFrom":makeQuery(id+"F45.opPattern","COPY",BODY,{"derivedFrom":makeQuery(id+"F44.opPattern","COPY",BODY,{"derivedFrom":makeQuery(id+"F27.opExtrude","SWEPT_BODY",BODY,{"disambiguationData":[OSD([sQuery(id+"F26.wireOp",EDGE,"E5.bottom"),sQuery(id+"F26.wireOp",EDGE,"E5.top"),sQuery(id+"F26.wireOp",EDGE,"E5.left"),sQuery(id+"F26.wireOp",EDGE,"E5.right")])]}),"instanceName":"1"}),"instanceName":"1"}),"instanceName":"1"}),"instanceName":"1"}),"instanceName":"1"}),"instanceName":"1"});
            transform(context, id + "F50", {"entities" : qUnion([Q0]), "transformType" : TransformType.TRANSLATION_3D, "dx" : 0 * mm, "dy" : -166 * mm, "dz" : 0 * mm, "makeCopy" : true});
        }
        {
            var Q0;
            Q0=makeQuery(id+"F50.opPattern","COPY",BODY,{"derivedFrom":makeQuery(id+"F49.opPattern","COPY",BODY,{"derivedFrom":makeQuery(id+"F48.opPattern","COPY",BODY,{"derivedFrom":makeQuery(id+"F47.opPattern","COPY",BODY,{"derivedFrom":makeQuery(id+"F46.opPattern","COPY",BODY,{"derivedFrom":makeQuery(id+"F45.opPattern","COPY",BODY,{"derivedFrom":makeQuery(id+"F44.opPattern","COPY",BODY,{"derivedFrom":makeQuery(id+"F27.opExtrude","SWEPT_BODY",BODY,{"disambiguationData":[OSD([sQuery(id+"F26.wireOp",EDGE,"E5.bottom"),sQuery(id+"F26.wireOp",EDGE,"E5.top"),sQuery(id+"F26.wireOp",EDGE,"E5.left"),sQuery(id+"F26.wireOp",EDGE,"E5.right")])]}),"instanceName":"1"}),"instanceName":"1"}),"instanceName":"1"}),"instanceName":"1"}),"instanceName":"1"}),"instanceName":"1"}),"instanceName":"1"});
            transform(context, id + "F51", {"entities" : qUnion([Q0]), "transformType" : TransformType.TRANSLATION_3D, "dx" : 0 * mm, "dy" : -166 * mm, "dz" : 0 * mm, "makeCopy" : true});
        }
        {
            var Q0;
            Q0=makeQuery(id+"F51.opPattern","COPY",BODY,{"derivedFrom":makeQuery(id+"F50.opPattern","COPY",BODY,{"derivedFrom":makeQuery(id+"F49.opPattern","COPY",BODY,{"derivedFrom":makeQuery(id+"F48.opPattern","COPY",BODY,{"derivedFrom":makeQuery(id+"F47.opPattern","COPY",BODY,{"derivedFrom":makeQuery(id+"F46.opPattern","COPY",BODY,{"derivedFrom":makeQuery(id+"F45.opPattern","COPY",BODY,{"derivedFrom":makeQuery(id+"F44.opPattern","COPY",BODY,{"derivedFrom":makeQuery(id+"F27.opExtrude","SWEPT_BODY",BODY,{"disambiguationData":[OSD([sQuery(id+"F26.wireOp",EDGE,"E5.bottom"),sQuery(id+"F26.wireOp",EDGE,"E5.top"),sQuery(id+"F26.wireOp",EDGE,"E5.left"),sQuery(id+"F26.wireOp",EDGE,"E5.right")])]}),"instanceName":"1"}),"instanceName":"1"}),"instanceName":"1"}),"instanceName":"1"}),"instanceName":"1"}),"instanceName":"1"}),"instanceName":"1"}),"instanceName":"1"});
            transform(context, id + "F52", {"entities" : qUnion([Q0]), "transformType" : TransformType.TRANSLATION_3D, "dx" : 0 * mm, "dy" : -166 * mm, "dz" : 0 * mm, "makeCopy" : true});
        }
        {
            var Q0;
            Q0=makeQuery(id+"F52.opPattern","COPY",BODY,{"derivedFrom":makeQuery(id+"F51.opPattern","COPY",BODY,{"derivedFrom":makeQuery(id+"F50.opPattern","COPY",BODY,{"derivedFrom":makeQuery(id+"F49.opPattern","COPY",BODY,{"derivedFrom":makeQuery(id+"F48.opPattern","COPY",BODY,{"derivedFrom":makeQuery(id+"F47.opPattern","COPY",BODY,{"derivedFrom":makeQuery(id+"F46.opPattern","COPY",BODY,{"derivedFrom":makeQuery(id+"F45.opPattern","COPY",BODY,{"derivedFrom":makeQuery(id+"F44.opPattern","COPY",BODY,{"derivedFrom":makeQuery(id+"F27.opExtrude","SWEPT_BODY",BODY,{"disambiguationData":[OSD([sQuery(id+"F26.wireOp",EDGE,"E5.bottom"),sQuery(id+"F26.wireOp",EDGE,"E5.top"),sQuery(id+"F26.wireOp",EDGE,"E5.left"),sQuery(id+"F26.wireOp",EDGE,"E5.right")])]}),"instanceName":"1"}),"instanceName":"1"}),"instanceName":"1"}),"instanceName":"1"}),"instanceName":"1"}),"instanceName":"1"}),"instanceName":"1"}),"instanceName":"1"}),"instanceName":"1"});
            transform(context, id + "F53", {"entities" : qUnion([Q0]), "transformType" : TransformType.TRANSLATION_3D, "dx" : 0 * mm, "dy" : -166 * mm, "dz" : 0 * mm, "makeCopy" : true});
        }
        {
            var Q0;
            Q0=makeQuery(id+"F53.opPattern","COPY",BODY,{"derivedFrom":makeQuery(id+"F52.opPattern","COPY",BODY,{"derivedFrom":makeQuery(id+"F51.opPattern","COPY",BODY,{"derivedFrom":makeQuery(id+"F50.opPattern","COPY",BODY,{"derivedFrom":makeQuery(id+"F49.opPattern","COPY",BODY,{"derivedFrom":makeQuery(id+"F48.opPattern","COPY",BODY,{"derivedFrom":makeQuery(id+"F47.opPattern","COPY",BODY,{"derivedFrom":makeQuery(id+"F46.opPattern","COPY",BODY,{"derivedFrom":makeQuery(id+"F45.opPattern","COPY",BODY,{"derivedFrom":makeQuery(id+"F44.opPattern","COPY",BODY,{"derivedFrom":makeQuery(id+"F27.opExtrude","SWEPT_BODY",BODY,{"disambiguationData":[OSD([sQuery(id+"F26.wireOp",EDGE,"E5.bottom"),sQuery(id+"F26.wireOp",EDGE,"E5.top"),sQuery(id+"F26.wireOp",EDGE,"E5.left"),sQuery(id+"F26.wireOp",EDGE,"E5.right")])]}),"instanceName":"1"}),"instanceName":"1"}),"instanceName":"1"}),"instanceName":"1"}),"instanceName":"1"}),"instanceName":"1"}),"instanceName":"1"}),"instanceName":"1"}),"instanceName":"1"}),"instanceName":"1"});
            transform(context, id + "F54", {"entities" : qUnion([Q0]), "transformType" : TransformType.TRANSLATION_3D, "dx" : 0 * mm, "dy" : -166 * mm, "dz" : 0 * mm, "makeCopy" : true});
        }
        {
            var Q0;
            Q0=makeQuery(id+"F17.opPattern","COPY",FACE,{"derivedFrom":makeQuery(id+"F15.opExtrude","SWEPT_FACE",FACE,{"disambiguationData":[OSD([sQuery(id+"F14.wireOp",EDGE,"E2.bottom")])]}),"instanceName":"1"});
            extrude(context, id + "F55", {"entities" : qUnion([Q0]), "operationType" : NewBodyOperationType.ADD, "depth" : 5 * mm});
        }
        {
            var Q0;
            Q0=makeQuery(id+"F19.opExtrude","SWEPT_FACE",FACE,{"disambiguationData":[OSD([sQuery(id+"F18.wireOp",EDGE,"E3.bottom")])]});
            extrude(context, id + "F56", {"entities" : qUnion([Q0]), "operationType" : NewBodyOperationType.ADD, "depth" : 5 * mm});
        }
        {
            var Q0;
            Q0=makeQuery(id+"F21.opPattern","COPY",FACE,{"derivedFrom":makeQuery(id+"F19.opExtrude","SWEPT_FACE",FACE,{"disambiguationData":[OSD([sQuery(id+"F18.wireOp",EDGE,"E3.bottom")])]}),"instanceName":"1"});
            extrude(context, id + "F57", {"entities" : qUnion([Q0]), "operationType" : NewBodyOperationType.ADD, "depth" : 5 * mm});
        }
        {
            var Q0;
            Q0=makeQuery(id+"F15.opExtrude","SWEPT_FACE",FACE,{"disambiguationData":[OSD([sQuery(id+"F14.wireOp",EDGE,"E2.bottom")])]});
            extrude(context, id + "F58", {"entities" : qUnion([Q0]), "operationType" : NewBodyOperationType.ADD, "depth" : 5 * mm});
        }
        {
            var Q0;
            Q0=makeQuery(id+"F4.opPattern","COPY",FACE,{"derivedFrom":makeQuery(id+"F2.opPattern","COPY",FACE,{"derivedFrom":makeQuery(id+"F1.opExtrude","CAP_FACE",FACE,{"disambiguationData":[OSD([sQuery(id+"F0.wireOp",EDGE,"E0.bottom"),sQuery(id+"F0.wireOp",EDGE,"E0.top"),sQuery(id+"F0.wireOp",EDGE,"E0.left"),sQuery(id+"F0.wireOp",EDGE,"E0.right")])],"isStart":false}),"instanceName":"1"}),"instanceName":"1"});
            var Q1;
            Q1=makeQuery(id+"F17.opPattern","COPY",BODY,{"derivedFrom":makeQuery(id+"F15.opExtrude","SWEPT_BODY",BODY,{"disambiguationData":[OSD([sQuery(id+"F14.wireOp",EDGE,"E2.bottom"),sQuery(id+"F14.wireOp",EDGE,"E2.top"),sQuery(id+"F14.wireOp",EDGE,"E2.left"),sQuery(id+"F14.wireOp",EDGE,"E2.right")])]}),"instanceName":"1"});
            extrude(context, id + "F59", {"entities" : qUnion([Q0]), "operationType" : NewBodyOperationType.ADD, "endBoundEntityBody" : qUnion([Q1]), "depth" : 5 * mm});
        }
        {
            var Q0;
            Q0=makeQuery(id+"F3.opPattern","COPY",FACE,{"derivedFrom":makeQuery(id+"F1.opExtrude","CAP_FACE",FACE,{"disambiguationData":[OSD([sQuery(id+"F0.wireOp",EDGE,"E0.bottom"),sQuery(id+"F0.wireOp",EDGE,"E0.top"),sQuery(id+"F0.wireOp",EDGE,"E0.left"),sQuery(id+"F0.wireOp",EDGE,"E0.right")])],"isStart":false}),"instanceName":"1"});
            var Q1;
            Q1=makeQuery(id+"F15.opExtrude","SWEPT_BODY",BODY,{"disambiguationData":[OSD([sQuery(id+"F14.wireOp",EDGE,"E2.bottom"),sQuery(id+"F14.wireOp",EDGE,"E2.top"),sQuery(id+"F14.wireOp",EDGE,"E2.left"),sQuery(id+"F14.wireOp",EDGE,"E2.right")])]});
            extrude(context, id + "F60", {"entities" : qUnion([Q0]), "operationType" : NewBodyOperationType.ADD, "endBoundEntityBody" : qUnion([Q1]), "depth" : 5 * mm});
        }
        {
            var Q0;
            Q0=makeQuery(id+"F1.opExtrude","CAP_FACE",FACE,{"disambiguationData":[OSD([sQuery(id+"F0.wireOp",EDGE,"E0.bottom"),sQuery(id+"F0.wireOp",EDGE,"E0.top"),sQuery(id+"F0.wireOp",EDGE,"E0.left"),sQuery(id+"F0.wireOp",EDGE,"E0.right")])],"isStart":false});
            extrude(context, id + "F61", {"entities" : qUnion([Q0]), "operationType" : NewBodyOperationType.ADD, "depth" : 5 * mm});
        }
        {
            var Q0;
            Q0=makeQuery(id+"F2.opPattern","COPY",FACE,{"derivedFrom":makeQuery(id+"F1.opExtrude","CAP_FACE",FACE,{"disambiguationData":[OSD([sQuery(id+"F0.wireOp",EDGE,"E0.bottom"),sQuery(id+"F0.wireOp",EDGE,"E0.top"),sQuery(id+"F0.wireOp",EDGE,"E0.left"),sQuery(id+"F0.wireOp",EDGE,"E0.right")])],"isStart":false}),"instanceName":"1"});
            extrude(context, id + "F62", {"entities" : qUnion([Q0]), "operationType" : NewBodyOperationType.ADD, "depth" : 5 * mm});
        }
        {
            var Q0;
            Q0=qCreatedBy(makeId("Top.planeOp"),FACE);
            var sketch = newSketch(context, id + "F63", { "sketchPlane" : qUnion([Q0])});
            skLineSegment(sketch, "E6.bottom", {"start": v(0, 0) * mm, "end": v(-48, 0) * mm});
            skLineSegment(sketch, "E6.top", {"start": v(0, -98) * mm, "end": v(-48, -98) * mm});
            skLineSegment(sketch, "E6.left", {"start": v(0, 0) * mm, "end": v(0, -98) * mm});
            skLineSegment(sketch, "E6.right", {"start": v(-48, 0) * mm, "end": v(-48, -98) * mm});
            skSolve(sketch);
        }
        {
            var Q0;
            Q0=makeQuery(id+"F63.imprint","IMPRINT",FACE,{"disambiguationData":[TD([[makeQuery(id+"F63.imprint","IMPRINT",EDGE,{"derivedFrom":sQuery(id+"F63.wireOp",EDGE,"E6.bottom")}),1.0]])]});
            extrude(context, id + "F64", {"entities" : qUnion([Q0]), "depth" : 2480 * mm, "offsetDistance" : 25 * mm});
        }
        {
            var Q0;
            Q0=qCreatedBy(makeId("Top.planeOp"),FACE);
            var sketch = newSketch(context, id + "F65", { "sketchPlane" : qUnion([Q0])});
            skLineSegment(sketch, "E7.bottom", {"start": v(-52.6, 0) * mm, "end": v(-100.6, 0) * mm});
            skLineSegment(sketch, "E7.top", {"start": v(-52.6, -48) * mm, "end": v(-100.6, -48) * mm});
            skLineSegment(sketch, "E7.left", {"start": v(-52.6, 0) * mm, "end": v(-52.6, -48) * mm});
            skLineSegment(sketch, "E7.right", {"start": v(-100.6, 0) * mm, "end": v(-100.6, -48) * mm});
            skSolve(sketch);
        }
        {
            var Q0;
            Q0=makeQuery(id+"F65.imprint","IMPRINT",FACE,{"disambiguationData":[TD([[makeQuery(id+"F65.imprint","IMPRINT",EDGE,{"derivedFrom":sQuery(id+"F65.wireOp",EDGE,"E7.bottom")}),1.0]])]});
            extrude(context, id + "F66", {"entities" : qUnion([Q0]), "depth" : 2480 * mm, "offsetDistance" : 25 * mm});
        }
        {
            var Q0;
            Q0=qCreatedBy(makeId("Front.planeOp"),FACE);
            var sketch = newSketch(context, id + "F67", { "sketchPlane" : qUnion([Q0])});
            skLineSegment(sketch, "E8.bottom", {"start": v(0, 0) * mm, "end": v(-28, 0) * mm});
            skLineSegment(sketch, "E8.top", {"start": v(0, -95) * mm, "end": v(-28, -95) * mm});
            skLineSegment(sketch, "E8.left", {"start": v(0, 0) * mm, "end": v(0, -95) * mm});
            skLineSegment(sketch, "E8.right", {"start": v(-28, 0) * mm, "end": v(-28, -95) * mm});
            skSolve(sketch);
        }
        {
            var Q0;
            Q0=qCreatedBy(makeId("Right.planeOp"),FACE);
            var sketch = newSketch(context, id + "F68", { "sketchPlane" : qUnion([Q0])});
            skLineSegment(sketch, "E9.bottom", {"start": v(0, 0) * mm, "end": v(-28, 0) * mm});
            skLineSegment(sketch, "E9.top", {"start": v(0, -95) * mm, "end": v(-28, -95) * mm});
            skLineSegment(sketch, "E9.left", {"start": v(0, 0) * mm, "end": v(0, -95) * mm});
            skLineSegment(sketch, "E9.right", {"start": v(-28, 0) * mm, "end": v(-28, -95) * mm});
            skSolve(sketch);
        }
        {
            var Q0;
            Q0=makeQuery(id+"F68.imprint","IMPRINT",FACE,{"disambiguationData":[TD([[makeQuery(id+"F68.imprint","IMPRINT",EDGE,{"derivedFrom":sQuery(id+"F68.wireOp",EDGE,"E9.bottom")}),1.0]])]});
            extrude(context, id + "F69", {"entities" : qUnion([Q0]), "depth" : 817 * mm, "offsetDistance" : 25 * mm});
        }
        {
            var Q0;
            Q0=makeQuery(id+"F67.imprint","IMPRINT",FACE,{"disambiguationData":[TD([[makeQuery(id+"F67.imprint","IMPRINT",EDGE,{"derivedFrom":sQuery(id+"F67.wireOp",EDGE,"E8.bottom")}),1.0]])]});
            extrude(context, id + "F70", {"entities" : qUnion([Q0]), "depth" : 2073 * mm, "offsetDistance" : 25 * mm});
        }
        {
            var Q0;
            Q0=makeQuery(id+"F66.opExtrude","SWEPT_FACE",FACE,{"disambiguationData":[OSD([sQuery(id+"F65.wireOp",EDGE,"E7.top")])]});
            var sketch = newSketch(context, id + "F71", { "sketchPlane" : qUnion([Q0])});
            skLineSegment(sketch, "E10.bottom", {"start": v(-100.6, 0) * mm, "end": v(-900.6, 0) * mm});
            skLineSegment(sketch, "E10.top", {"start": v(-100.6, -90) * mm, "end": v(-900.6, -90) * mm});
            skLineSegment(sketch, "E10.left", {"start": v(-100.6, 0) * mm, "end": v(-100.6, -90) * mm});
            skLineSegment(sketch, "E10.right", {"start": v(-900.6, 0) * mm, "end": v(-900.6, -90) * mm});
            skSolve(sketch);
        }
        {
            var Q0;
            Q0=makeQuery(id+"F71.imprint","IMPRINT",FACE,{"disambiguationData":[TD([[makeQuery(id+"F71.imprint","IMPRINT",EDGE,{"derivedFrom":sQuery(id+"F71.wireOp",EDGE,"E10.bottom")}),1.0]])]});
            extrude(context, id + "F72", {"entities" : qUnion([Q0]), "depth" : 2000 * mm, "offsetDistance" : 25 * mm});
        }
        {
            var Q0;
            Q0=makeQuery(id+"F72.opExtrude","SWEPT_EDGE",EDGE,{"disambiguationData":[OSD([sQuery(id+"F71.wireOp",EDGE,"E10.bottom"),sQuery(id+"F71.wireOp",EDGE,"E10.right")])]});
            var Q1;
            Q1=makeQuery(id+"F72.opExtrude","SWEPT_EDGE",EDGE,{"disambiguationData":[OSD([sQuery(id+"F71.wireOp",EDGE,"E10.top"),sQuery(id+"F71.wireOp",EDGE,"E10.right")])]});
            var Q2;
            Q2=makeQuery(id+"F72.opExtrude","CAP_EDGE",EDGE,{"disambiguationData":[OSD([sQuery(id+"F71.wireOp",EDGE,"E10.right")])],"isStart":true});
            var Q3;
            Q3=makeQuery(id+"F72.opExtrude","CAP_EDGE",EDGE,{"disambiguationData":[OSD([sQuery(id+"F71.wireOp",EDGE,"E10.bottom")])],"isStart":true});
            var Q4;
            Q4=makeQuery(id+"F72.opExtrude","CAP_EDGE",EDGE,{"disambiguationData":[OSD([sQuery(id+"F71.wireOp",EDGE,"E10.top")])],"isStart":true});
            var Q5;
            Q5=makeQuery(id+"F72.opExtrude","CAP_EDGE",EDGE,{"disambiguationData":[OSD([sQuery(id+"F71.wireOp",EDGE,"E10.right")])],"isStart":false});
            var Q6;
            Q6=makeQuery(id+"F72.opExtrude","CAP_EDGE",EDGE,{"disambiguationData":[OSD([sQuery(id+"F71.wireOp",EDGE,"E10.bottom")])],"isStart":false});
            var Q7;
            Q7=makeQuery(id+"F72.opExtrude","CAP_EDGE",EDGE,{"disambiguationData":[OSD([sQuery(id+"F71.wireOp",EDGE,"E10.top")])],"isStart":false});
            var Q8;
            Q8=makeQuery(id+"F72.opExtrude","CAP_EDGE",EDGE,{"disambiguationData":[OSD([sQuery(id+"F71.wireOp",EDGE,"E10.left")])],"isStart":false});
            var Q9;
            Q9=makeQuery(id+"F72.opExtrude","SWEPT_EDGE",EDGE,{"disambiguationData":[OSD([sQuery(id+"F65.wireOp",EDGE,"E7.top"),sQuery(id+"F65.wireOp",EDGE,"E7.right"),sQuery(id+"F71.wireOp",EDGE,"E10.bottom"),sQuery(id+"F71.wireOp",EDGE,"E10.left")])]});
            var Q10;
            Q10=makeQuery(id+"F72.opExtrude","SWEPT_EDGE",EDGE,{"disambiguationData":[OSD([sQuery(id+"F71.wireOp",EDGE,"E10.top"),sQuery(id+"F71.wireOp",EDGE,"E10.left")])]});
            var Q11;
            Q11=makeQuery(id+"F72.opExtrude","CAP_EDGE",EDGE,{"disambiguationData":[OSD([sQuery(id+"F71.wireOp",EDGE,"E10.left")])],"isStart":true});
            fillet(context, id + "F73", {"entities" : qUnion([Q0, Q1, Q2, Q3, Q4, Q5, Q6, Q7, Q8, Q9, Q10, Q11]), "radius" : 10 * mm, "tangentPropagation" : true, "allowEdgeOverflow" : false});
        }
        {
            var Q0;
            Q0=makeQuery(id+"F65.imprint","IMPRINT",FACE,{"disambiguationData":[TD([[makeQuery(id+"F65.imprint","IMPRINT",EDGE,{"derivedFrom":sQuery(id+"F65.wireOp",EDGE,"E7.bottom")}),1.0]])]});
            extrude(context, id + "F74", {"entities" : qUnion([Q0]), "oppositeDirection" : true, "depth" : 1230 * mm, "offsetDistance" : 25 * mm});
        }
        {
            var Q0;
            Q0=makeQuery(id+"F68.imprint","IMPRINT",FACE,{"disambiguationData":[TD([[makeQuery(id+"F68.imprint","IMPRINT",EDGE,{"derivedFrom":sQuery(id+"F68.wireOp",EDGE,"E9.bottom")}),1.0]])]});
            extrude(context, id + "F75", {"entities" : qUnion([Q0]), "oppositeDirection" : true, "depth" : 777 * mm, "offsetDistance" : 25 * mm});
        }
        {
            var Q0;
            Q0=makeQuery(id+"F68.imprint","IMPRINT",FACE,{"disambiguationData":[TD([[makeQuery(id+"F68.imprint","IMPRINT",EDGE,{"derivedFrom":sQuery(id+"F68.wireOp",EDGE,"E9.bottom")}),1.0]])]});
            extrude(context, id + "F76", {"entities" : qUnion([Q0]), "oppositeDirection" : true, "depth" : 364.5 * mm, "offsetDistance" : 25 * mm});
        }
        {
            var Q0;
            Q0=qCreatedBy(makeId("Front.planeOp"),FACE);
            var sketch = newSketch(context, id + "F77", { "sketchPlane" : qUnion([Q0])});
            skLineSegment(sketch, "E11.bottom", {"start": v(-1322.64, 0) * mm, "end": v(-1370.64, 0) * mm});
            skLineSegment(sketch, "E11.top", {"start": v(-1322.64, -95) * mm, "end": v(-1370.64, -95) * mm});
            skLineSegment(sketch, "E11.left", {"start": v(-1322.64, 0) * mm, "end": v(-1322.64, -95) * mm});
            skLineSegment(sketch, "E11.right", {"start": v(-1370.64, 0) * mm, "end": v(-1370.64, -95) * mm});
            skSolve(sketch);
        }
        {
            var Q0;
            Q0=makeQuery(id+"F77.imprint","IMPRINT",FACE,{"disambiguationData":[TD([[makeQuery(id+"F77.imprint","IMPRINT",EDGE,{"derivedFrom":sQuery(id+"F77.wireOp",EDGE,"E11.bottom")}),1.0]])]});
            extrude(context, id + "F78", {"entities" : qUnion([Q0]), "depth" : 8.5 * mm, "offsetDistance" : 25 * mm});
        }
        {
            var Q0;
            Q0=makeQuery(id+"F68.imprint","IMPRINT",FACE,{"disambiguationData":[TD([[makeQuery(id+"F68.imprint","IMPRINT",EDGE,{"derivedFrom":sQuery(id+"F68.wireOp",EDGE,"E9.bottom")}),1.0]])]});
            extrude(context, id + "F79", {"entities" : qUnion([Q0]), "oppositeDirection" : true, "depth" : 432.5 * mm, "offsetDistance" : 25 * mm});
        }
    });
